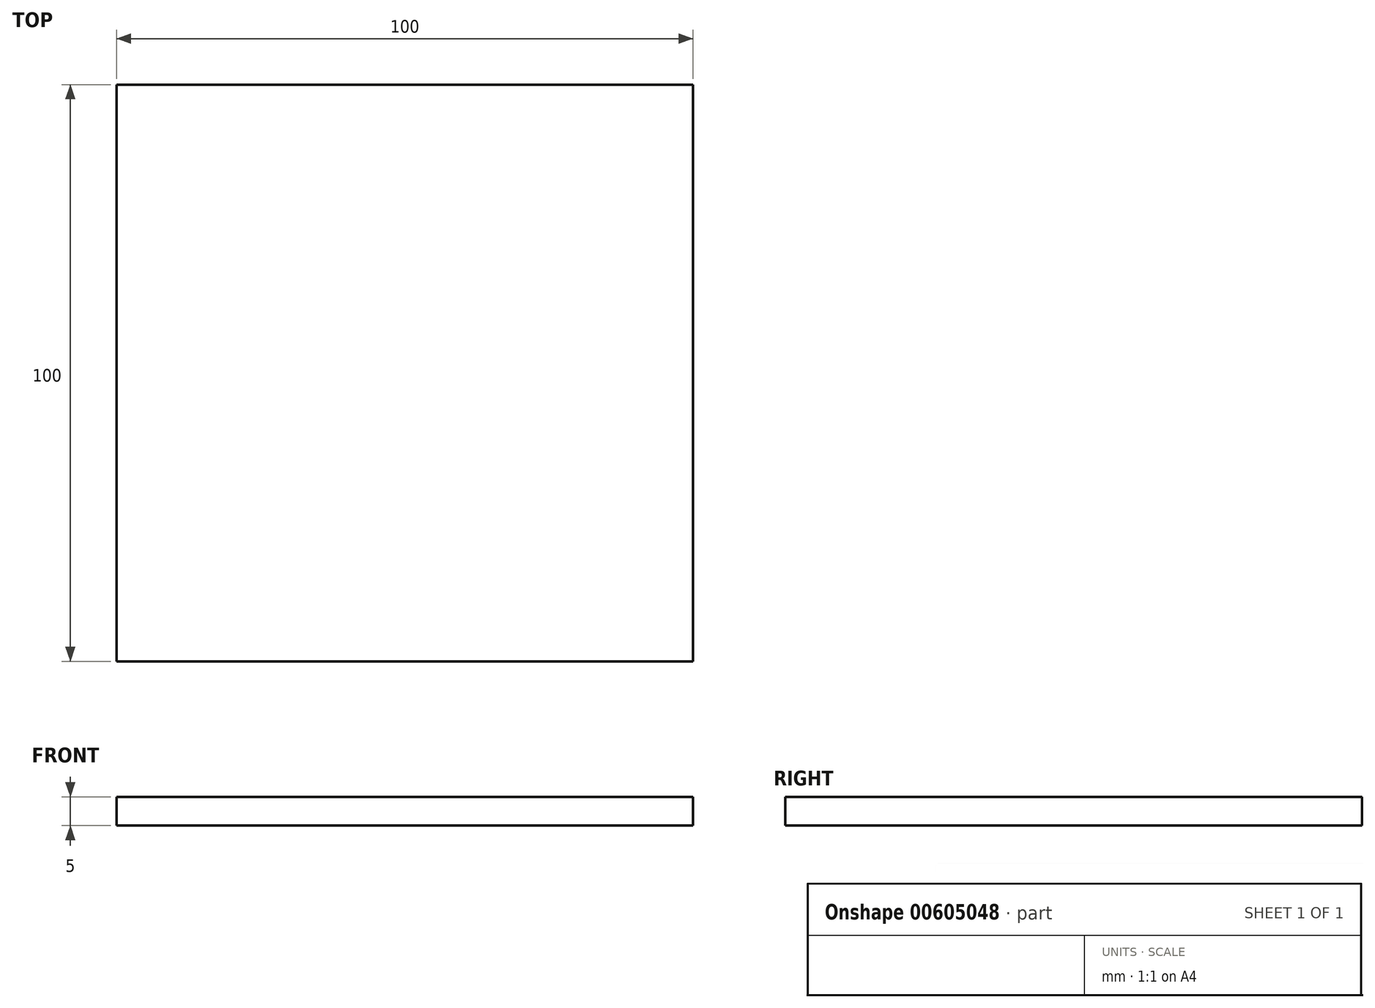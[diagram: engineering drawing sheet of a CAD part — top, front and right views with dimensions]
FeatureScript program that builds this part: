
annotation { "Feature Type Name" : "Feature", "Feature Type Description" : "" }
export const myFeature = defineFeature(function(context is Context, id is Id, definition is map)
    precondition{}
    {
        {
            var Q0;
            Q0=qCreatedBy(makeId("Top.planeOp"),FACE);
            var sketch = newSketch(context, id + "F0", { "sketchPlane" : qUnion([Q0])});
            skLineSegment(sketch, "E0.bottom", {"start": v(50, -50) * mm, "end": v(-50, -50) * mm});
            skLineSegment(sketch, "E0.top", {"start": v(50, 50) * mm, "end": v(-50, 50) * mm});
            skLineSegment(sketch, "E0.left", {"start": v(50, -50) * mm, "end": v(50, 50) * mm});
            skLineSegment(sketch, "E0.right", {"start": v(-50, -50) * mm, "end": v(-50, 50) * mm});
            skPoint(sketch, "E0.middle", {"position": v(0, 0) * mm});
            skSolve(sketch);
        }
        {
            var Q0;
            Q0 = qSketchRegion(id + "F0", true);
            var Q1;
            Q1=makeQuery(id+"F0.imprint","IMPRINT",FACE,{"disambiguationData":[TD([[makeQuery(id+"F0.imprint","IMPRINT",EDGE,{"derivedFrom":sQuery(id+"F0.wireOp",EDGE,"E0.bottom")}),-1.0]])]});
            extrude(context, id + "F1", {"entities" : qUnion([Q0, Q1]), "oppositeDirection" : true, "depth" : 5 * mm, "offsetDistance" : 25 * mm});
        }
    });
